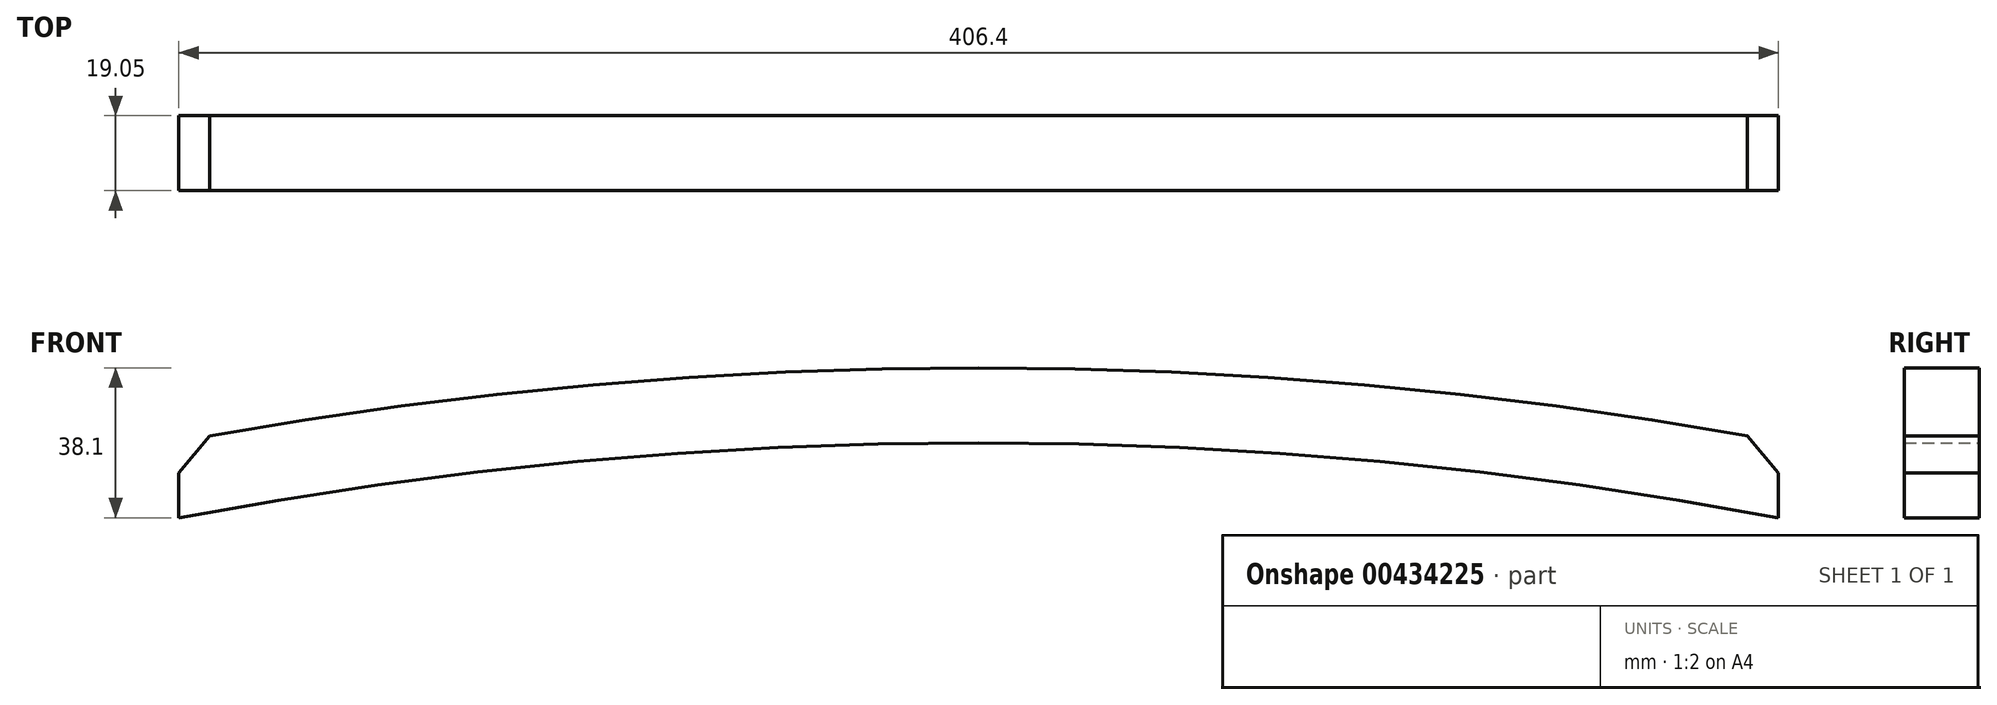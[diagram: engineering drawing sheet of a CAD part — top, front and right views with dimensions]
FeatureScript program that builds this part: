
annotation { "Feature Type Name" : "Feature", "Feature Type Description" : "" }
export const myFeature = defineFeature(function(context is Context, id is Id, definition is map)
    precondition{}
    {
        {
            var Q0;
            Q0=qCreatedBy(makeId("Front.planeOp"),FACE);
            var sketch = newSketch(context, id + "F0", { "sketchPlane" : qUnion([Q0])});
            skLineSegment(sketch, "E0", {"start": v(-203.2, -19.05) * mm, "end": v(203.2, -19.05) * mm, "construction": true});
            skLineSegment(sketch, "E1", {"start": v(0, 0) * mm, "end": v(0, -19.05) * mm, "construction": true});
            skPoint(sketch, "E1.startSnap0", {"position": v(0, -19.05) * mm});
            skArc(sketch, "E2", {"start": v(203.2, -19.05) * mm, "mid": v(0, 0) * mm, "end": v(-203.2, -19.05) * mm});
            skLineSegment(sketch, "E3", {"start": v(-203.2, 19.05) * mm, "end": v(203.2, 19.05) * mm, "construction": true});
            skArc(sketch, "E4.trimOffspring", {"start": v(203.2, 0.33) * mm, "mid": v(0, 19.05) * mm, "end": v(-203.2, 0.33) * mm});
            skLineSegment(sketch, "E5", {"start": v(-203.2, -19.05) * mm, "end": v(-203.2, 0.33) * mm});
            skLineSegment(sketch, "E6", {"start": v(-203.2, 19.05) * mm, "end": v(-203.2, 0.33) * mm, "construction": true});
            skLineSegment(sketch, "E7", {"start": v(203.2, 19.05) * mm, "end": v(203.2, 0.33) * mm, "construction": true});
            skLineSegment(sketch, "E8", {"start": v(203.2, 0.33) * mm, "end": v(203.2, -19.05) * mm});
            skSolve(sketch);
        }
        {
            var Q0;
            Q0 = qSketchRegion(id + "F0", true);
            extrude(context, id + "F1", {"entities" : qUnion([Q0]), "depth" : 19.05 * mm});
        }
        {
            var Q0;
            Q0=makeQuery(id+"F1.opExtrude","SWEPT_EDGE",EDGE,{"disambiguationData":[OSD([sQuery(id+"F0.wireOp",EDGE,"E4.trimOffspring"),sQuery(id+"F0.wireOp",EDGE,"E5")])]});
            var Q1;
            Q1=makeQuery(id+"F1.opExtrude","SWEPT_EDGE",EDGE,{"disambiguationData":[OSD([sQuery(id+"F0.wireOp",EDGE,"E4.trimOffspring"),sQuery(id+"F0.wireOp",EDGE,"E8")])]});
            chamfer(context, id + "F2", {"entities" : qUnion([Q0, Q1]), "width" : 9.52 * mm, "tangentPropagation" : true});
        }
    });
